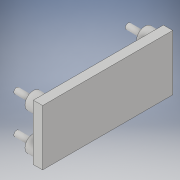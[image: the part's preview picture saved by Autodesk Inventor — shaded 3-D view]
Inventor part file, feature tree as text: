
AUTODESK INVENTOR PART (.ipt)
format: ipt  version: 2019 (Build 230136000, 136)  size: 161,792 bytes
history: native  units: mm
features: sketch x6, extrude x4, other x1
ambient origin geometry x8: Origin, YZ Plane, XZ Plane, XY Plane, X Axis, Y Axis, Z Axis, Center Point
bodies: Body1 (feature_tree)
feature tree (11):
  other  "ソリッド1"
  sketch  "スケッチ1"
  extrude  "押し出し1"  Depth=60.0mm
  extrude  "押し出し2"  Depth=140.0mm
  sketch  "スケッチ4"
  sketch  "スケッチ5"
  extrude  "押し出し3"  Depth=10.0mm TaperAngle=0.0deg
  extrude  "押し出し4"  Depth=18.0mm
  sketch  "スケッチ2"
  sketch  "スケッチ3"
  sketch  "スケッチ6"
